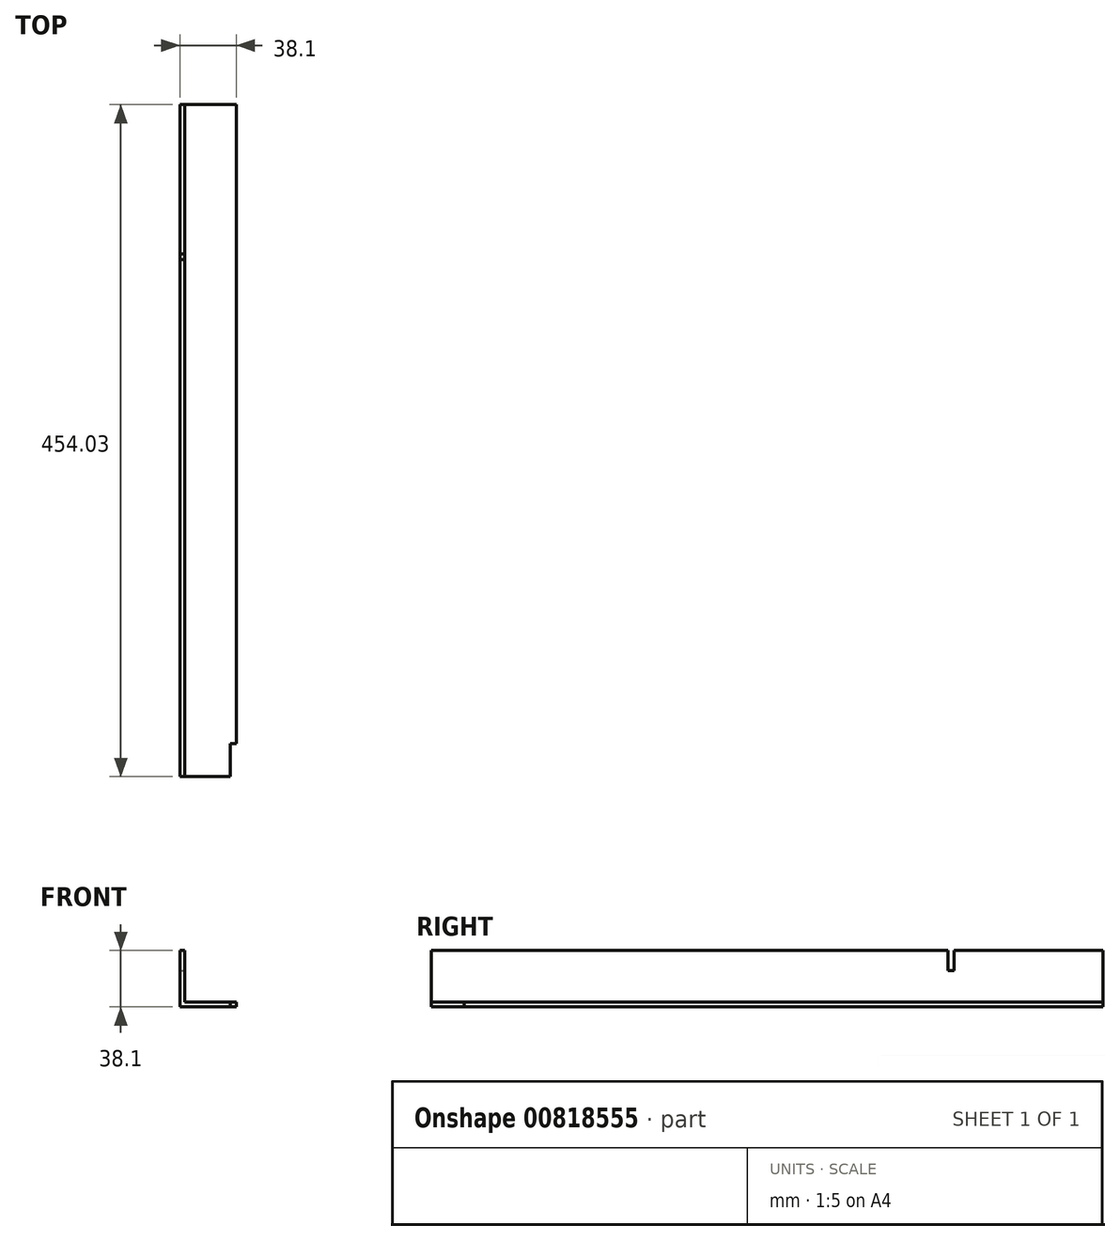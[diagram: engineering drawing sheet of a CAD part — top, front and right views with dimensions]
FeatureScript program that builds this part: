
annotation { "Feature Type Name" : "Feature", "Feature Type Description" : "" }
export const myFeature = defineFeature(function(context is Context, id is Id, definition is map)
    precondition{}
    {
        {
            var Q0;
            Q0=qCreatedBy(makeId("Front.planeOp"),FACE);
            var sketch = newSketch(context, id + "F0", { "sketchPlane" : qUnion([Q0])});
            skLineSegment(sketch, "E0", {"start": v(-21.73, 20.45) * mm, "end": v(-21.73, -17.65) * mm});
            skLineSegment(sketch, "E1", {"start": v(-21.73, -17.65) * mm, "end": v(16.37, -17.65) * mm});
            skLineSegment(sketch, "E2", {"start": v(16.37, -17.65) * mm, "end": v(16.37, -14.47) * mm});
            skLineSegment(sketch, "E3", {"start": v(16.37, -14.47) * mm, "end": v(-18.55, -14.47) * mm});
            skLineSegment(sketch, "E4", {"start": v(-18.55, -14.47) * mm, "end": v(-18.55, 20.45) * mm});
            skLineSegment(sketch, "E5", {"start": v(-18.55, 20.45) * mm, "end": v(-21.73, 20.45) * mm});
            skSolve(sketch);
        }
        {
            var Q0;
            Q0=makeQuery(id+"F0.imprint","IMPRINT",FACE,{"disambiguationData":[TD([[makeQuery(id+"F0.imprint","IMPRINT",EDGE,{"derivedFrom":sQuery(id+"F0.wireOp",EDGE,"E0")}),1.0]])]});
            extrude(context, id + "F1", {"entities" : qUnion([Q0]), "depth" : 454.02 * mm, "offsetDistance" : 25.4 * mm});
        }
        {
            var Q0;
            Q0=makeQuery(id+"F1.opExtrude","SWEPT_FACE",FACE,{"disambiguationData":[OSD([sQuery(id+"F0.wireOp",EDGE,"E1")])]});
            var sketch = newSketch(context, id + "F2", { "sketchPlane" : qUnion([Q0])});
            skLineSegment(sketch, "E6", {"start": v(16.37, 454.03) * mm, "end": v(12.4, 454.03) * mm});
            skLineSegment(sketch, "E7", {"start": v(12.4, 454.03) * mm, "end": v(12.4, 431.8) * mm});
            skLineSegment(sketch, "E8", {"start": v(12.4, 431.8) * mm, "end": v(16.37, 431.8) * mm});
            skLineSegment(sketch, "E9", {"start": v(16.37, 431.8) * mm, "end": v(16.37, 454.03) * mm});
            skSolve(sketch);
        }
        {
            var Q0;
            Q0 = qSketchRegion(id + "F2", true);
            extrude(context, id + "F3", {"entities" : qUnion([Q0]), "operationType" : NewBodyOperationType.REMOVE, "oppositeDirection" : true, "depth" : 25.4 * mm, "offsetDistance" : 25.4 * mm});
        }
        {
            var Q0;
            Q0=makeQuery(id+"F1.opExtrude","SWEPT_FACE",FACE,{"disambiguationData":[OSD([sQuery(id+"F0.wireOp",EDGE,"E4")])]});
            var sketch = newSketch(context, id + "F4", { "sketchPlane" : qUnion([Q0])});
            skLineSegment(sketch, "E10", {"start": v(-100.8, 20.45) * mm, "end": v(-100.8, 6.96) * mm});
            skLineSegment(sketch, "E11", {"start": v(-100.8, 6.96) * mm, "end": v(-104.78, 6.96) * mm});
            skLineSegment(sketch, "E12", {"start": v(-104.78, 6.96) * mm, "end": v(-104.78, 20.45) * mm});
            skLineSegment(sketch, "E13", {"start": v(-104.78, 20.45) * mm, "end": v(-100.8, 20.45) * mm});
            skSolve(sketch);
        }
        {
            var Q0;
            Q0 = qSketchRegion(id + "F4", true);
            extrude(context, id + "F5", {"entities" : qUnion([Q0]), "operationType" : NewBodyOperationType.REMOVE, "oppositeDirection" : true, "depth" : 25.4 * mm, "offsetDistance" : 25.4 * mm});
        }
    });
